# Revit family: Receptor_Sani-Flor_9_Inch_Shallow_Top-Zurn-Z1970
name_source: partatom
category: Plumbing Fixtures
units: mm (PartAtom-declared; Revit-internal decimal feet)

## family parameters
Always vertical = Yes
Cut with Voids When Loaded = No
Maintain Annotation Orientation = No
OmniClass Number = 23.45.55.21
OmniClass Title = Drains (Wastes)
Part Type = Normal
Room Calculation Point = No
Round Connector Dimension = Use Radius
Shared = No
Work Plane-Based = No

## types (12) — shared parameters
Approx. Weight (Lbs) = 28.00 lb
Assembly Code = D2030300
Bottom Dia = 12 "
CW Connection = No
Default Elevation = 20 "
Description = 9 [229] DIAMETER TOP SHALLOW A.R.C. SANI-FLOR RECEPTOR
Grate Dia = 8.063 "
Grate Open Area (Sq. In) = 18.00 in²
HW Connection = No
Inside Radius = 4.25 "
Main Material = Cast Iron- Zurn- White A.R.E Coated- Interior
Manufacturer = Zurn Water, LLC
Manufacurer Brand = Zurn
Modified Date = 03/06/2026
Product Documentation Link = https://files.zurn.com
Product Page URL = https://www.zurn.com
Product data url = https://www.bimobject.com
Top Dia = 9 "
Top Plate Radius = 4.5 "
URL = www.zurn.com
Vent Connection = No
WFU = 1
Waste Connection = Yes
ZN_Frame Dia = 9.688 "
zero-valued in all types: CWFU, HWFU

## per-type parameters (varying)
| type | Body Height_E | Connector Radius | Frame & Grate Material | Frame Height | Model | Model line Dia | Pipe Size_A Inside Diameter | Pipe Size_A Inside Radius | Pipe Size_A Nominal Diameter | Pipe Size_A Outer Diameter | Pipe Size_A Outer Radius | Top Inside Dia | Top Inside Radius | Type Comments |
| Z1970-2" NH Outlet | 4.75 " | 1 " | Cast Iron- Zurn- White A.R.E Coated- Interior | 2 " | Z1970 | 9 " | 2.067 " | 1.034 " | 2 " | 2.375 " | 1.188 " | 8.5 " | 4.25 " | Z1970- 2 Inch No-Hub Outlet |
| Z1970-2" NL Outlet | 3.5 " | 1 " | Cast Iron- Zurn- White A.R.E Coated- Interior | 2 " | Z1970 | 9 " | 2.067 " | 1.034 " | 2 " | 2.375 " | 1.188 " | 8.5 " | 4.25 " | Z1970- 2 Inch Neo-Loc Outlet |
| Z1970-3" NH Outlet | 4.75 " | 1.5 " | Cast Iron- Zurn- White A.R.E Coated- Interior | 2 " | Z1970 | 9 " | 3.068 " | 1.534 " | 3 " | 3.5 " | 1.75 " | 8.5 " | 4.25 " | Z1970- 3 Inch No-Hub Outlet |
| Z1970-3" NL Outlet | 3.5 " | 1.5 " | Cast Iron- Zurn- White A.R.E Coated- Interior | 2 " | Z1970 | 9 " | 3.068 " | 1.534 " | 3 " | 3.5 " | 1.75 " | 8.5 " | 4.25 " | Z1970- 3 Inch Neo-Loc Outlet |
| Z1970-4" NH Outlet | 4.75 " | 2 " | Cast Iron- Zurn- White A.R.E Coated- Interior | 2 " | Z1970 | 9 " | 4.026 " | 2.013 " | 4 " | 4.5 " | 2.25 " | 8.5 " | 4.25 " | Z1970- 4 Inch No-Hub Outlet |
| Z1970-4" NL Outlet | 3.5 " | 2 " | Cast Iron- Zurn- White A.R.E Coated- Interior | 2 " | Z1970 | 9 " | 4.026 " | 2.013 " | 4 " | 4.5 " | 2.25 " | 8.5 " | 4.25 " | Z1970- 4 Inch Neo-Loc Outlet |
| ZN1970-2" NH Outlet | 4.75 " | 1 " | Bronze - Zurn - Polished Nickel | 2.188 " | ZN1970 | 9.688 " | 2.067 " | 1.034 " | 2 " | 2.375 " | 1.188 " | 8.688 " | 4.344 " | ZN1970- 2 Inch No-Hub Outlet |
| ZN1970-2" NL Outlet | 3.5 " | 1 " | Bronze - Zurn - Polished Nickel | 2.188 " | ZN1970 | 9.688 " | 2.067 " | 1.034 " | 2 " | 2.375 " | 1.188 " | 8.688 " | 4.344 " | ZN1970- 2 Inch Neo-Loc Outlet |
| ZN1970-3" NH Outlet | 4.75 " | 1.5 " | Bronze - Zurn - Polished Nickel | 2.188 " | ZN1970 | 9.688 " | 3.068 " | 1.534 " | 3 " | 3.5 " | 1.75 " | 8.688 " | 4.344 " | ZN1970- 3 Inch No-Hub Outlet |
| ZN1970-3" NL Outlet | 3.5 " | 1.5 " | Bronze - Zurn - Polished Nickel | 2.188 " | ZN1970 | 9.688 " | 3.068 " | 1.534 " | 3 " | 3.5 " | 1.75 " | 8.688 " | 4.344 " | ZN1970- 3 Inch Neo-Loc Outlet |
| ZN1970-4" NH Outlet | 4.75 " | 2 " | Bronze - Zurn - Polished Nickel | 2.188 " | ZN1970 | 9.688 " | 4.026 " | 2.013 " | 4 " | 4.5 " | 2.25 " | 8.688 " | 4.344 " | ZN1970- 4 Inch No-Hub Outlet |
| ZN1970-4" NL Outlet | 3.5 " | 2 " | Bronze - Zurn - Polished Nickel | 2.188 " | ZN1970 | 9.688 " | 4.026 " | 2.013 " | 4 " | 4.5 " | 2.25 " | 8.688 " | 4.344 " | ZN1970- 4 Inch Neo-Loc Outlet |

## geometry (parser evidence)
native form markers: Blend x4, Sweep x4
no freeform markers — native parametric forms only
